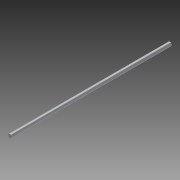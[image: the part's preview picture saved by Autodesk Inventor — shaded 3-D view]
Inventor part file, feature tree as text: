
AUTODESK INVENTOR PART (.ipt)
format: ipt  version: 2014 (Build 180170000, 170)  size: 70,656 bytes
history: native  units: in
note: dims shown in document units (in); Inventor stores cm internally (conversion verified against a paired STEP export)
features: extrude x1, sketch x1
ambient origin geometry x8: Origin, YZ Plane, XZ Plane, XY Plane, X Axis, Y Axis, Z Axis, Center Point
bodies: Solid1 (feature_tree)
feature tree (2):
  extrude  "Extrusion1"  Depth=24.0in TaperAngle=0.0deg
  sketch  "Sketch1"  dims[d0=0.5in d1=24.0in d2=0.0in]
